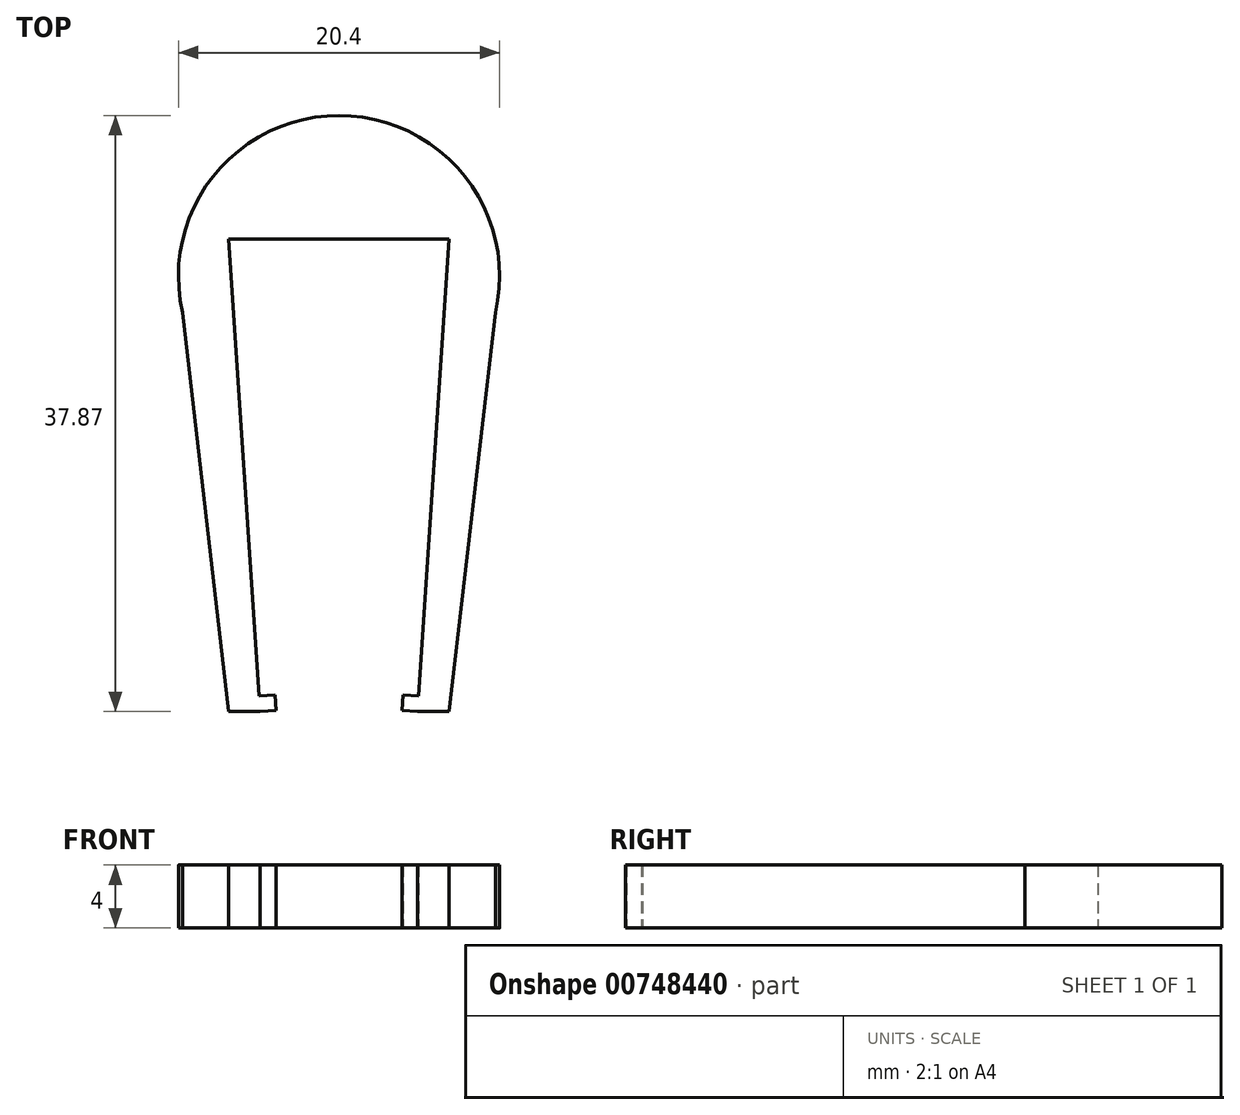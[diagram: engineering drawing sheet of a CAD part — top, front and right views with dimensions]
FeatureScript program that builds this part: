
annotation { "Feature Type Name" : "Feature", "Feature Type Description" : "" }
export const myFeature = defineFeature(function(context is Context, id is Id, definition is map)
    precondition{}
    {
        {
            var Q0;
            Q0=qCreatedBy(makeId("Top.planeOp"),FACE);
            var sketch = newSketch(context, id + "F0", { "sketchPlane" : qUnion([Q0])});
            skPoint(sketch, "E0.middle", {"position": v(0, 0) * mm});
            skPoint(sketch, "E1", {"position": v(-7, 15) * mm});
            skPoint(sketch, "E2", {"position": v(7, 15) * mm});
            skPoint(sketch, "E3", {"position": v(7, -15) * mm});
            skPoint(sketch, "E4", {"position": v(-7, -15) * mm});
            skLineSegment(sketch, "E5", {"start": v(-7, 15) * mm, "end": v(7, 15) * mm});
            skPoint(sketch, "E6", {"position": v(-5, -15) * mm});
            skPoint(sketch, "E7", {"position": v(5, -15) * mm});
            skLineSegment(sketch, "E8", {"start": v(-7, 15) * mm, "end": v(-5.07, -14) * mm});
            skLineSegment(sketch, "E9", {"start": v(7, 15) * mm, "end": v(5.07, -14) * mm});
            skPoint(sketch, "E10.centerSnap0", {"position": v(0, 15) * mm});
            skLineSegment(sketch, "E11", {"start": v(-5, -15) * mm, "end": v(-7, -15) * mm});
            skLineSegment(sketch, "E12", {"start": v(5, -15) * mm, "end": v(7, -15) * mm});
            skLineSegment(sketch, "E13", {"start": v(-7, -15) * mm, "end": v(-9.93, 10.35) * mm});
            skLineSegment(sketch, "E14", {"start": v(7, -15) * mm, "end": v(9.93, 10.35) * mm});
            skArc(sketch, "E15", {"start": v(9.93, 10.35) * mm, "mid": v(0, 22.87) * mm, "end": v(-9.93, 10.35) * mm});
            skPoint(sketch, "E10.center.orphan", {"position": v(0, 11.5) * mm});
            skLineSegment(sketch, "E16", {"start": v(-5, -15) * mm, "end": v(-4, -14.93) * mm});
            skLineSegment(sketch, "E17", {"start": v(-4, -14.93) * mm, "end": v(-4.07, -13.94) * mm});
            skLineSegment(sketch, "E18", {"start": v(-4.07, -13.94) * mm, "end": v(-5.07, -14) * mm});
            skLineSegment(sketch, "E19", {"start": v(0, 15) * mm, "end": v(0, -14.93) * mm, "construction": true});
            skLineSegment(sketch, "E20.MirrorCS", {"start": v(4.07, -13.94) * mm, "end": v(5.07, -14) * mm});
            skLineSegment(sketch, "E21.MirrorCS", {"start": v(4, -14.93) * mm, "end": v(4.07, -13.94) * mm});
            skLineSegment(sketch, "E22.MirrorCS", {"start": v(5, -15) * mm, "end": v(4, -14.93) * mm});
            skSolve(sketch);
        }
        {
            var Q0;
            Q0=makeQuery(id+"F0.imprint","IMPRINT",FACE,{"disambiguationData":[TD([[makeQuery(id+"F0.imprint","IMPRINT",EDGE,{"derivedFrom":sQuery(id+"F0.wireOp",EDGE,"E5")}),1.0]])]});
            extrude(context, id + "F1", {"entities" : qUnion([Q0]), "depth" : 4 * mm, "offsetDistance" : 25 * mm});
        }
    });
